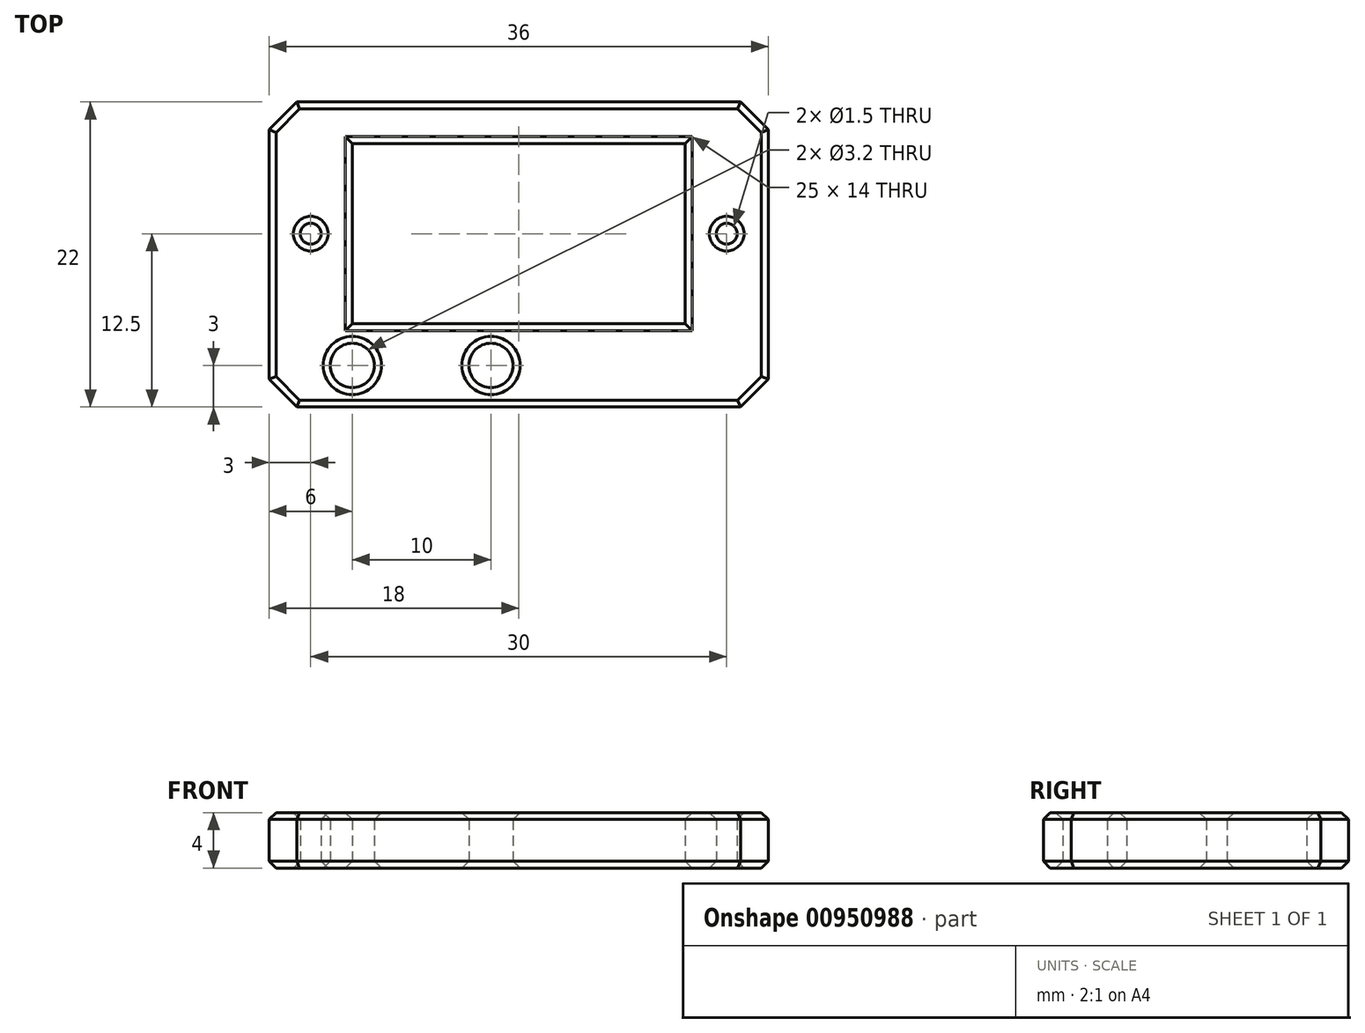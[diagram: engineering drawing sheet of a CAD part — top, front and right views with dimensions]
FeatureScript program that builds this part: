
annotation { "Feature Type Name" : "Feature", "Feature Type Description" : "" }
export const myFeature = defineFeature(function(context is Context, id is Id, definition is map)
    precondition{}
    {
        {
            var Q0;
            Q0=qCreatedBy(makeId("Top.planeOp"),FACE);
            var sketch = newSketch(context, id + "F0", { "sketchPlane" : qUnion([Q0])});
            skLineSegment(sketch, "E0.bottom", {"start": v(0, 0) * mm, "end": v(24, 0) * mm});
            skLineSegment(sketch, "E0.top", {"start": v(0, 13) * mm, "end": v(24, 13) * mm});
            skLineSegment(sketch, "E0.left", {"start": v(0, 0) * mm, "end": v(0, 13) * mm});
            skLineSegment(sketch, "E0.right", {"start": v(24, 0) * mm, "end": v(24, 13) * mm});
            skLineSegment(sketch, "E1.bottom", {"start": v(-6, -6) * mm, "end": v(30, -6) * mm});
            skLineSegment(sketch, "E1.top", {"start": v(-6, 16) * mm, "end": v(30, 16) * mm});
            skLineSegment(sketch, "E1.left", {"start": v(-6, -6) * mm, "end": v(-6, 16) * mm});
            skLineSegment(sketch, "E1.right", {"start": v(30, -6) * mm, "end": v(30, 16) * mm});
            skCircle(sketch, "E2", {"center": v(0, -3) * mm, "radius": 1.6 * mm});
            skLineSegment(sketch, "E3", {"start": v(-12.03, -3) * mm, "end": v(35.96, -3) * mm, "construction": true});
            skCircle(sketch, "E4", {"center": v(10, -3) * mm, "radius": 1.6 * mm});
            skLineSegment(sketch, "E5", {"start": v(-3, 22.73) * mm, "end": v(-3, -20.57) * mm, "construction": true});
            skLineSegment(sketch, "E6", {"start": v(27, 22.22) * mm, "end": v(27, -9.22) * mm, "construction": true});
            skCircle(sketch, "E7", {"center": v(-3, 6.5) * mm, "radius": 0.75 * mm});
            skCircle(sketch, "E8", {"center": v(27, 6.5) * mm, "radius": 0.75 * mm});
            skSolve(sketch);
        }
        {
            var Q0;
            Q0=makeQuery(id+"F0.imprint","IMPRINT",FACE,{"disambiguationData":[TD([[makeQuery(id+"F0.imprint","IMPRINT",EDGE,{"derivedFrom":sQuery(id+"F0.wireOp",EDGE,"E0.bottom")}),-1.0]])]});
            extrude(context, id + "F1", {"entities" : qUnion([Q0]), "depth" : 4 * mm, "offsetDistance" : 25 * mm});
        }
        {
            var Q0;
            Q0=makeQuery(id+"F1.opExtrude","SWEPT_EDGE",EDGE,{"disambiguationData":[OSD([sQuery(id+"F0.wireOp",EDGE,"E1.bottom"),sQuery(id+"F0.wireOp",EDGE,"E1.left")])]});
            var Q1;
            Q1=makeQuery(id+"F1.opExtrude","SWEPT_EDGE",EDGE,{"disambiguationData":[OSD([sQuery(id+"F0.wireOp",EDGE,"E1.bottom"),sQuery(id+"F0.wireOp",EDGE,"E1.right")])]});
            var Q2;
            Q2=makeQuery(id+"F1.opExtrude","SWEPT_EDGE",EDGE,{"disambiguationData":[OSD([sQuery(id+"F0.wireOp",EDGE,"E1.top"),sQuery(id+"F0.wireOp",EDGE,"E1.right")])]});
            var Q3;
            Q3=makeQuery(id+"F1.opExtrude","SWEPT_EDGE",EDGE,{"disambiguationData":[OSD([sQuery(id+"F0.wireOp",EDGE,"E1.top"),sQuery(id+"F0.wireOp",EDGE,"E1.left")])]});
            chamfer(context, id + "F2", {"entities" : qUnion([Q0, Q1, Q2, Q3]), "width" : 2 * mm, "tangentPropagation" : true});
        }
        {
            var Q0;
            Q0=makeQuery(id+"F1.opExtrude","CAP_FACE",FACE,{"disambiguationData":[OSD([sQuery(id+"F0.wireOp",EDGE,"E0.bottom"),sQuery(id+"F0.wireOp",EDGE,"E0.top"),sQuery(id+"F0.wireOp",EDGE,"E0.left"),sQuery(id+"F0.wireOp",EDGE,"E0.right"),sQuery(id+"F0.wireOp",EDGE,"E1.bottom"),sQuery(id+"F0.wireOp",EDGE,"E1.top"),sQuery(id+"F0.wireOp",EDGE,"E1.left"),sQuery(id+"F0.wireOp",EDGE,"E1.right"),sQuery(id+"F0.wireOp",EDGE,"E2"),sQuery(id+"F0.wireOp",EDGE,"E4"),sQuery(id+"F0.wireOp",EDGE,"E7"),sQuery(id+"F0.wireOp",EDGE,"E8")])],"isStart":true});
            var Q1;
            Q1=makeQuery(id+"F1.opExtrude","CAP_FACE",FACE,{"disambiguationData":[OSD([sQuery(id+"F0.wireOp",EDGE,"E0.bottom"),sQuery(id+"F0.wireOp",EDGE,"E0.top"),sQuery(id+"F0.wireOp",EDGE,"E0.left"),sQuery(id+"F0.wireOp",EDGE,"E0.right"),sQuery(id+"F0.wireOp",EDGE,"E1.bottom"),sQuery(id+"F0.wireOp",EDGE,"E1.top"),sQuery(id+"F0.wireOp",EDGE,"E1.left"),sQuery(id+"F0.wireOp",EDGE,"E1.right"),sQuery(id+"F0.wireOp",EDGE,"E2"),sQuery(id+"F0.wireOp",EDGE,"E4"),sQuery(id+"F0.wireOp",EDGE,"E7"),sQuery(id+"F0.wireOp",EDGE,"E8")])],"isStart":false});
            chamfer(context, id + "F3", {"entities" : qUnion([Q0, Q1]), "width" : 0.5 * mm, "tangentPropagation" : true});
        }
    });
